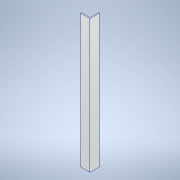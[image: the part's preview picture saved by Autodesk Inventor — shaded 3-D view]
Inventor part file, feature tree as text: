
AUTODESK INVENTOR PART (.ipt)
format: ipt  version: 2022 (Build 260153000, 153)  size: 99,840 bytes
history: native  units: mm
features: extrude x1, sketch x1
ambient origin geometry x8: Origin, YZ Plane, XZ Plane, XY Plane, X Axis, Y Axis, Z Axis, Center Point
bodies: Solid1 (feature_tree)
feature tree (2):
  extrude  "Extrusion1"  Depth=50.0mm
  sketch  "Sketch1"  dims[d0=50.0mm d1=50.0mm d2=5.0mm d3=5.0mm d4=700.0mm d5=0.0mm d6=0.5mm d7=0.872665mm d8=0.5mm d9=0.872665mm]
